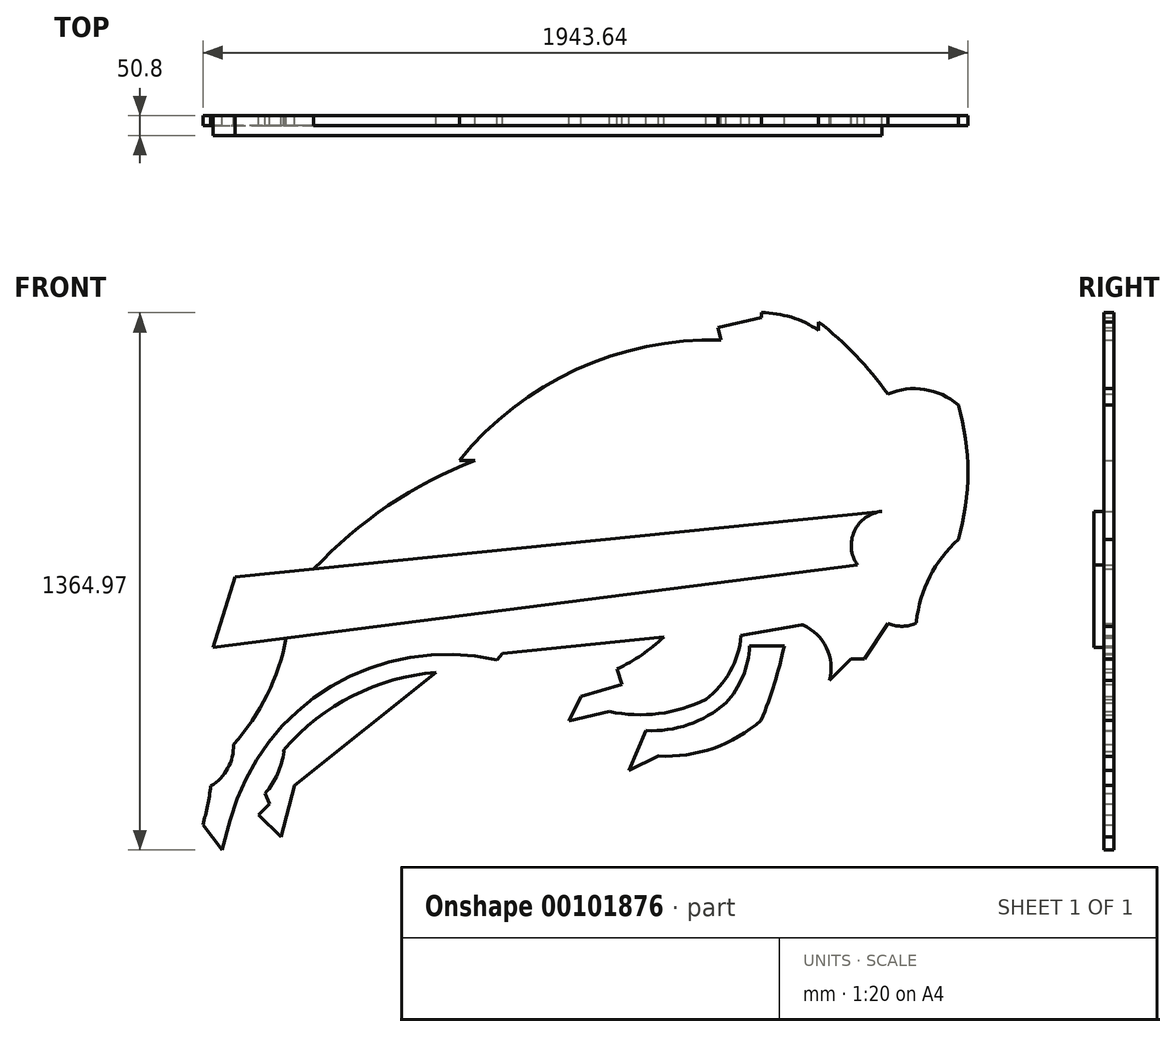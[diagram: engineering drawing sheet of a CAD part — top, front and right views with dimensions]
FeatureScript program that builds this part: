
annotation { "Feature Type Name" : "Feature", "Feature Type Description" : "" }
export const myFeature = defineFeature(function(context is Context, id is Id, definition is map)
    precondition{}
    {
        {
            var Q0;
            Q0=qCreatedBy(makeId("Front.planeOp"),FACE);
            var sketch = newSketch(context, id + "F0", { "sketchPlane" : qUnion([Q0])});
            skLineSegment(sketch, "E0", {"start": v(-973.64, 129.34) * mm, "end": v(-1030.7, -49.44) * mm});
            skLineSegment(sketch, "E1", {"start": v(-1030.7, -49.44) * mm, "end": v(606.92, 160.33) * mm});
            skLineSegment(sketch, "E2", {"start": v(-973.64, 129.34) * mm, "end": v(668.91, 296.17) * mm});
            skArc(sketch, "E3", {"start": v(668.91, 296.17) * mm, "mid": v(598.96, 246.03) * mm, "end": v(606.92, 160.33) * mm});
            skSolve(sketch);
        }
        {
            var Q0;
            Q0 = qSketchRegion(id + "F0", true);
            extrude(context, id + "F1", {"entities" : qUnion([Q0]), "depth" : 50.8 * mm});
        }
        {
            var Q0;
            Q0=makeQuery(id+"F1.opExtrude","CAP_FACE",FACE,{"disambiguationData":[OSD([sQuery(id+"F0.wireOp",EDGE,"E0"),sQuery(id+"F0.wireOp",EDGE,"E1"),sQuery(id+"F0.wireOp",EDGE,"E2"),sQuery(id+"F0.wireOp",EDGE,"E3")])],"isStart":false});
            var sketch = newSketch(context, id + "F2", { "sketchPlane" : qUnion([Q0])});
            skArc(sketch, "E4", {"start": v(260.08, 731.48) * mm, "mid": v(-108.02, 656.23) * mm, "end": v(-404.4, 425.33) * mm});
            skArc(sketch, "E5", {"start": v(-978.1, -295.87) * mm, "mid": v(-892.88, -169.79) * mm, "end": v(-844.3, -25.57) * mm});
            skArc(sketch, "E6", {"start": v(-1035.95, -401.48) * mm, "mid": v(-992.78, -356.48) * mm, "end": v(-978.1, -295.87) * mm});
            skLineSegment(sketch, "E7", {"start": v(-1006.96, -563.83) * mm, "end": v(-986.67, -488.45) * mm});
            skArc(sketch, "E8", {"start": v(-309.17, -81.5) * mm, "mid": v(-730, -148.32) * mm, "end": v(-986.67, -488.45) * mm});
            skLineSegment(sketch, "E9", {"start": v(-1006.96, -563.83) * mm, "end": v(-1056.25, -500.05) * mm});
            skArc(sketch, "E10", {"start": v(-1056.25, -500.05) * mm, "mid": v(-1044.13, -451.17) * mm, "end": v(-1035.95, -401.48) * mm});
            skLineSegment(sketch, "E11", {"start": v(-309.17, -81.5) * mm, "end": v(-295.02, -64.52) * mm});
            skLineSegment(sketch, "E12", {"start": v(-295.02, -64.52) * mm, "end": v(114.91, -22.89) * mm});
            skArc(sketch, "E13", {"start": v(-3.55, -103.77) * mm, "mid": v(58.9, -68.04) * mm, "end": v(114.91, -22.89) * mm});
            skLineSegment(sketch, "E14", {"start": v(-3.55, -103.77) * mm, "end": v(8.03, -143.56) * mm});
            skLineSegment(sketch, "E15", {"start": v(8.03, -143.56) * mm, "end": v(-95.54, -173.7) * mm});
            skLineSegment(sketch, "E16", {"start": v(-95.54, -173.7) * mm, "end": v(-126.44, -236.65) * mm});
            skLineSegment(sketch, "E17", {"start": v(-126.44, -236.65) * mm, "end": v(-23, -212.52) * mm});
            skArc(sketch, "E18", {"start": v(-23, -212.52) * mm, "mid": v(102, -217.48) * mm, "end": v(221.8, -181.49) * mm});
            skArc(sketch, "E19", {"start": v(221.8, -181.49) * mm, "mid": v(283.47, -109.79) * mm, "end": v(311.44, -19.44) * mm});
            skLineSegment(sketch, "E20", {"start": v(311.44, -19.44) * mm, "end": v(464.74, 7.81) * mm});
            skArc(sketch, "E21", {"start": v(535.54, -133.22) * mm, "mid": v(528.3, -50.32) * mm, "end": v(468.37, 7.4) * mm});
            skPoint(sketch, "E22.visualSharp", {"position": v(466.59, 8.14) * mm});
            skArc(sketch, "E22.filletArc", {"start": v(468.37, 7.4) * mm, "mid": v(466.58, 7.87) * mm, "end": v(464.74, 7.81) * mm});
            skLineSegment(sketch, "E23", {"start": v(535.54, -133.22) * mm, "end": v(590.7, -78.05) * mm});
            skLineSegment(sketch, "E24", {"start": v(590.7, -78.05) * mm, "end": v(625.19, -78.05) * mm});
            skLineSegment(sketch, "E25", {"start": v(625.19, -78.05) * mm, "end": v(683.8, 11.6) * mm});
            skArc(sketch, "E26", {"start": v(683.8, 11.6) * mm, "mid": v(717.53, 4.59) * mm, "end": v(751.58, 9.86) * mm});
            skArc(sketch, "E27", {"start": v(863.08, 224.87) * mm, "mid": v(790.65, 130.36) * mm, "end": v(756.67, 16.25) * mm});
            skPoint(sketch, "E28.visualSharp", {"position": v(756.2, 11.6) * mm});
            skArc(sketch, "E28.filletArc", {"start": v(751.58, 9.86) * mm, "mid": v(755.05, 12.32) * mm, "end": v(756.67, 16.25) * mm});
            skArc(sketch, "E29", {"start": v(863.08, 224.87) * mm, "mid": v(887.4, 395.78) * mm, "end": v(863.08, 566.69) * mm});
            skArc(sketch, "E30", {"start": v(863.08, 566.69) * mm, "mid": v(777.39, 606.14) * mm, "end": v(683.8, 594.27) * mm});
            skArc(sketch, "E31", {"start": v(683.8, 594.27) * mm, "mid": v(602.68, 692.55) * mm, "end": v(507.96, 777.8) * mm});
            skLineSegment(sketch, "E32", {"start": v(507.96, 777.8) * mm, "end": v(507.96, 756.32) * mm});
            skArc(sketch, "E33", {"start": v(507.96, 756.32) * mm, "mid": v(438.89, 789.48) * mm, "end": v(363.15, 801.14) * mm});
            skLineSegment(sketch, "E34", {"start": v(363.15, 801.14) * mm, "end": v(363.15, 788.44) * mm});
            skLineSegment(sketch, "E35", {"start": v(363.15, 788.44) * mm, "end": v(252.82, 763.21) * mm});
            skLineSegment(sketch, "E36", {"start": v(252.82, 763.21) * mm, "end": v(260.08, 731.48) * mm});
            skLineSegment(sketch, "E37", {"start": v(-404.4, 425.33) * mm, "end": v(-364.33, 425.33) * mm});
            skArc(sketch, "E38", {"start": v(-364.33, 425.33) * mm, "mid": v(-585.07, 310.89) * mm, "end": v(-774.28, 149.6) * mm});
            skSolve(sketch);
        }
        {
            var Q0;
            Q0 = qSketchRegion(id + "F2", true);
            var Q1;
            Q1=makeQuery(id+"F2.imprint","IMPRINT",FACE,{"disambiguationData":[TD([[makeQuery(id+"F2.imprint","IMPRINT",EDGE,{"derivedFrom":sQuery(id+"F2.wireOp",EDGE,"E4")}),1.0]])]});
            extrude(context, id + "F3", {"entities" : qUnion([Q0, Q1]), "depth" : 25.4 * mm});
        }
        {
            var Q0;
            Q0=makeQuery(id+"F1.opExtrude","CAP_FACE",FACE,{"disambiguationData":[OSD([sQuery(id+"F0.wireOp",EDGE,"E0"),sQuery(id+"F0.wireOp",EDGE,"E1"),sQuery(id+"F0.wireOp",EDGE,"E2"),sQuery(id+"F0.wireOp",EDGE,"E3")])],"isStart":false});
            var sketch = newSketch(context, id + "F4", { "sketchPlane" : qUnion([Q0])});
            skLineSegment(sketch, "E39", {"start": v(-973.64, 129.34) * mm, "end": v(-1030.7, -49.44) * mm});
            skLineSegment(sketch, "E40", {"start": v(-1030.7, -49.44) * mm, "end": v(606.92, 160.33) * mm});
            skLineSegment(sketch, "E41", {"start": v(-973.64, 129.34) * mm, "end": v(668.91, 296.17) * mm});
            skArc(sketch, "E42", {"start": v(668.91, 296.17) * mm, "mid": v(598.96, 246.03) * mm, "end": v(606.92, 160.33) * mm});
            skSolve(sketch);
        }
        {
            var Q0;
            Q0 = qSketchRegion(id + "F4", true);
            extrude(context, id + "F5", {"entities" : qUnion([Q0]), "depth" : 50.8 * mm});
        }
        {
            var Q0;
            Q0=makeQuery(id+"F1.opExtrude","CAP_FACE",FACE,{"disambiguationData":[OSD([sQuery(id+"F0.wireOp",EDGE,"E0"),sQuery(id+"F0.wireOp",EDGE,"E1"),sQuery(id+"F0.wireOp",EDGE,"E2"),sQuery(id+"F0.wireOp",EDGE,"E3")])],"isStart":true});
            var sketch = newSketch(context, id + "F6", { "sketchPlane" : qUnion([Q0])});
            skLineSegment(sketch, "E43", {"start": v(-668.91, 296.17) * mm, "end": v(973.64, 129.34) * mm});
            skLineSegment(sketch, "E44", {"start": v(973.64, 129.34) * mm, "end": v(1030.7, -49.44) * mm});
            skLineSegment(sketch, "E45", {"start": v(1030.7, -49.44) * mm, "end": v(-606.92, 160.33) * mm});
            skArc(sketch, "E46", {"start": v(-606.92, 160.33) * mm, "mid": v(-598.96, 246.03) * mm, "end": v(-668.91, 296.17) * mm});
            skSolve(sketch);
        }
        {
            var Q0;
            Q0=makeQuery(id+"F6.imprint","IMPRINT",FACE,{"disambiguationData":[TD([[makeQuery(id+"F6.imprint","IMPRINT",EDGE,{"derivedFrom":sQuery(id+"F6.wireOp",EDGE,"E43")}),1.0]])]});
            extrude(context, id + "F7", {"entities" : qUnion([Q0]), "operationType" : NewBodyOperationType.REMOVE, "oppositeDirection" : true, "depth" : 50.8 * mm});
        }
        {
            var Q0;
            Q0=makeQuery(id+"F3.opExtrude","CAP_FACE",FACE,{"disambiguationData":[OSD([sQuery(id+"F0.wireOp",EDGE,"E1"),sQuery(id+"F0.wireOp",EDGE,"E2"),sQuery(id+"F0.wireOp",EDGE,"E3"),sQuery(id+"F2.wireOp",EDGE,"E4"),sQuery(id+"F2.wireOp",EDGE,"E5"),sQuery(id+"F2.wireOp",EDGE,"E6"),sQuery(id+"F2.wireOp",EDGE,"E7"),sQuery(id+"F2.wireOp",EDGE,"E8"),sQuery(id+"F2.wireOp",EDGE,"E9"),sQuery(id+"F2.wireOp",EDGE,"E10"),sQuery(id+"F2.wireOp",EDGE,"E11"),sQuery(id+"F2.wireOp",EDGE,"E12"),sQuery(id+"F2.wireOp",EDGE,"E13"),sQuery(id+"F2.wireOp",EDGE,"E14"),sQuery(id+"F2.wireOp",EDGE,"E15"),sQuery(id+"F2.wireOp",EDGE,"E16"),sQuery(id+"F2.wireOp",EDGE,"E17"),sQuery(id+"F2.wireOp",EDGE,"E18"),sQuery(id+"F2.wireOp",EDGE,"E19"),sQuery(id+"F2.wireOp",EDGE,"E20"),sQuery(id+"F2.wireOp",EDGE,"E21"),sQuery(id+"F2.wireOp",EDGE,"E22.filletArc"),sQuery(id+"F2.wireOp",EDGE,"E23"),sQuery(id+"F2.wireOp",EDGE,"E24"),sQuery(id+"F2.wireOp",EDGE,"E25"),sQuery(id+"F2.wireOp",EDGE,"E26"),sQuery(id+"F2.wireOp",EDGE,"E27"),sQuery(id+"F2.wireOp",EDGE,"E28.filletArc"),sQuery(id+"F2.wireOp",EDGE,"E29"),sQuery(id+"F2.wireOp",EDGE,"E30"),sQuery(id+"F2.wireOp",EDGE,"E31"),sQuery(id+"F2.wireOp",EDGE,"E32"),sQuery(id+"F2.wireOp",EDGE,"E33"),sQuery(id+"F2.wireOp",EDGE,"E34"),sQuery(id+"F2.wireOp",EDGE,"E35"),sQuery(id+"F2.wireOp",EDGE,"E36"),sQuery(id+"F2.wireOp",EDGE,"E37"),sQuery(id+"F2.wireOp",EDGE,"E38")])],"isStart":true});
            var sketch = newSketch(context, id + "F8", { "sketchPlane" : qUnion([Q0])});
            skArc(sketch, "E47", {"start": v(848.7, -307.72) * mm, "mid": v(675.35, -172.47) * mm, "end": v(463.75, -112.7) * mm});
            skLineSegment(sketch, "E48", {"start": v(463.75, -112.7) * mm, "end": v(823.31, -399.79) * mm});
            skLineSegment(sketch, "E49", {"start": v(823.31, -399.79) * mm, "end": v(857.97, -531.17) * mm});
            skLineSegment(sketch, "E50", {"start": v(857.97, -531.17) * mm, "end": v(914.31, -474.82) * mm});
            skLineSegment(sketch, "E51", {"start": v(914.31, -474.82) * mm, "end": v(886.14, -446.64) * mm});
            skPoint(sketch, "E51.endSnap0", {"position": v(886.14, -503) * mm});
            skLineSegment(sketch, "E52", {"start": v(886.14, -446.64) * mm, "end": v(897.64, -419.94) * mm});
            skPoint(sketch, "E53.visualSharp", {"position": v(851.18, -310.6) * mm});
            skArc(sketch, "E53.filletArc", {"start": v(850.43, -314.15) * mm, "mid": v(850.31, -310.73) * mm, "end": v(848.7, -307.72) * mm});
            skArc(sketch, "E54", {"start": v(850.43, -314.15) * mm, "mid": v(866.26, -370.52) * mm, "end": v(897.64, -419.94) * mm});
            skArc(sketch, "E55", {"start": v(-333.12, -45.55) * mm, "mid": v(-315.58, -123.35) * mm, "end": v(-272.34, -190.36) * mm});
            skLineSegment(sketch, "E56", {"start": v(-69.25, -260.42) * mm, "end": v(-26.92, -361.34) * mm});
            skLineSegment(sketch, "E57", {"start": v(-26.92, -361.34) * mm, "end": v(-101.8, -325.53) * mm});
            skLineSegment(sketch, "E58", {"start": v(-333.12, -45.55) * mm, "end": v(-420.84, -45.55) * mm});
            skArc(sketch, "E59", {"start": v(-420.84, -45.55) * mm, "mid": v(-395.92, -141.32) * mm, "end": v(-362.24, -234.37) * mm});
            skArc(sketch, "E60", {"start": v(-362.24, -234.37) * mm, "mid": v(-240.92, -305.37) * mm, "end": v(-101.8, -325.53) * mm});
            skPoint(sketch, "E61", {"position": v(-272.34, -190.36) * mm});
            skArc(sketch, "E62", {"start": v(-272.34, -190.36) * mm, "mid": v(-177.66, -245.3) * mm, "end": v(-69.25, -260.42) * mm});
            skSolve(sketch);
        }
        {
            var Q0;
            Q0 = qSketchRegion(id + "F8", true);
            extrude(context, id + "F9", {"entities" : qUnion([Q0]), "depth" : 25.4 * mm});
        }
        {
            var Q0;
            Q0=makeQuery(id+"F9.opExtrude","CAP_FACE",FACE,{"disambiguationData":[OSD([sQuery(id+"F8.wireOp",EDGE,"E47"),sQuery(id+"F8.wireOp",EDGE,"E48"),sQuery(id+"F8.wireOp",EDGE,"E49"),sQuery(id+"F8.wireOp",EDGE,"E50"),sQuery(id+"F8.wireOp",EDGE,"E51"),sQuery(id+"F8.wireOp",EDGE,"E52"),sQuery(id+"F8.wireOp",EDGE,"E53.filletArc"),sQuery(id+"F8.wireOp",EDGE,"E54")])],"isStart":true});
            var sketch = newSketch(context, id + "F10", { "sketchPlane" : qUnion([Q0])});
            skArc(sketch, "E63.0", {"start": v(-463.75, -112.7) * mm, "mid": v(-675.35, -172.47) * mm, "end": v(-848.7, -307.72) * mm});
            skLineSegment(sketch, "E63.1", {"start": v(-823.31, -399.79) * mm, "end": v(-463.75, -112.7) * mm});
            skArc(sketch, "E63.2", {"start": v(-848.7, -307.72) * mm, "mid": v(-850.31, -310.73) * mm, "end": v(-850.43, -314.15) * mm});
            skLineSegment(sketch, "E63.3", {"start": v(-857.97, -531.17) * mm, "end": v(-823.31, -399.79) * mm});
            skArc(sketch, "E63.4", {"start": v(-850.43, -314.15) * mm, "mid": v(-866.26, -370.52) * mm, "end": v(-897.64, -419.94) * mm});
            skLineSegment(sketch, "E63.5", {"start": v(-897.64, -419.94) * mm, "end": v(-886.14, -446.64) * mm});
            skLineSegment(sketch, "E63.6", {"start": v(-886.14, -446.64) * mm, "end": v(-914.31, -474.82) * mm});
            skLineSegment(sketch, "E63.7", {"start": v(-914.31, -474.82) * mm, "end": v(-857.97, -531.17) * mm});
            skLineSegment(sketch, "E64.0", {"start": v(420.84, -45.55) * mm, "end": v(333.12, -45.55) * mm});
            skArc(sketch, "E64.1", {"start": v(362.24, -234.37) * mm, "mid": v(395.92, -141.32) * mm, "end": v(420.84, -45.55) * mm});
            skArc(sketch, "E64.2", {"start": v(272.34, -190.36) * mm, "mid": v(177.66, -245.3) * mm, "end": v(69.25, -260.42) * mm});
            skLineSegment(sketch, "E64.3", {"start": v(69.25, -260.42) * mm, "end": v(26.92, -361.34) * mm});
            skLineSegment(sketch, "E64.4", {"start": v(26.92, -361.34) * mm, "end": v(101.8, -325.53) * mm});
            skArc(sketch, "E64.5", {"start": v(333.12, -45.55) * mm, "mid": v(315.58, -123.35) * mm, "end": v(272.34, -190.36) * mm});
            skArc(sketch, "E64.6", {"start": v(101.8, -325.53) * mm, "mid": v(240.92, -305.37) * mm, "end": v(362.24, -234.37) * mm});
            skSolve(sketch);
        }
        {
            var Q0;
            Q0=makeQuery(id+"F10.imprint","IMPRINT",FACE,{"disambiguationData":[TD([[makeQuery(id+"F10.imprint","IMPRINT",EDGE,{"derivedFrom":sQuery(id+"F10.wireOp",EDGE,"E63.0")}),-1.0]])]});
            var Q1;
            Q1=makeQuery(id+"F10.imprint","IMPRINT",FACE,{"disambiguationData":[TD([[makeQuery(id+"F10.imprint","IMPRINT",EDGE,{"derivedFrom":sQuery(id+"F10.wireOp",EDGE,"E64.0")}),1.0]])]});
            extrude(context, id + "F11", {"entities" : qUnion([Q0, Q1]), "depth" : 25.4 * mm});
        }
        {
            var Q0;
            Q0=makeQuery(id+"F9.opExtrude","CAP_FACE",FACE,{"disambiguationData":[OSD([sQuery(id+"F8.wireOp",EDGE,"E47"),sQuery(id+"F8.wireOp",EDGE,"E48"),sQuery(id+"F8.wireOp",EDGE,"E49"),sQuery(id+"F8.wireOp",EDGE,"E50"),sQuery(id+"F8.wireOp",EDGE,"E51"),sQuery(id+"F8.wireOp",EDGE,"E52"),sQuery(id+"F8.wireOp",EDGE,"E53.filletArc"),sQuery(id+"F8.wireOp",EDGE,"E54")])],"isStart":false});
            var sketch = newSketch(context, id + "F12", { "sketchPlane" : qUnion([Q0])});
            skArc(sketch, "E65.0", {"start": v(897.64, -419.94) * mm, "mid": v(866.26, -370.52) * mm, "end": v(850.43, -314.15) * mm});
            skLineSegment(sketch, "E65.1", {"start": v(886.14, -446.64) * mm, "end": v(897.64, -419.94) * mm});
            skArc(sketch, "E65.2", {"start": v(850.43, -314.15) * mm, "mid": v(850.31, -310.73) * mm, "end": v(848.7, -307.72) * mm});
            skLineSegment(sketch, "E65.3", {"start": v(914.31, -474.82) * mm, "end": v(886.14, -446.64) * mm});
            skArc(sketch, "E65.4", {"start": v(848.7, -307.72) * mm, "mid": v(675.35, -172.47) * mm, "end": v(463.75, -112.7) * mm});
            skLineSegment(sketch, "E65.5", {"start": v(463.75, -112.7) * mm, "end": v(823.31, -399.79) * mm});
            skLineSegment(sketch, "E65.6", {"start": v(823.31, -399.79) * mm, "end": v(857.97, -531.17) * mm});
            skLineSegment(sketch, "E65.7", {"start": v(857.97, -531.17) * mm, "end": v(914.31, -474.82) * mm});
            skArc(sketch, "E66.0", {"start": v(-69.25, -260.42) * mm, "mid": v(-177.66, -245.3) * mm, "end": v(-272.34, -190.36) * mm});
            skLineSegment(sketch, "E66.1", {"start": v(-26.92, -361.34) * mm, "end": v(-69.25, -260.42) * mm});
            skLineSegment(sketch, "E66.2", {"start": v(-333.12, -45.55) * mm, "end": v(-420.84, -45.55) * mm});
            skArc(sketch, "E66.3", {"start": v(-420.84, -45.55) * mm, "mid": v(-395.92, -141.32) * mm, "end": v(-362.24, -234.37) * mm});
            skArc(sketch, "E66.4", {"start": v(-362.24, -234.37) * mm, "mid": v(-240.92, -305.37) * mm, "end": v(-101.8, -325.53) * mm});
            skArc(sketch, "E66.5", {"start": v(-272.34, -190.36) * mm, "mid": v(-315.58, -123.35) * mm, "end": v(-333.12, -45.55) * mm});
            skLineSegment(sketch, "E66.6", {"start": v(-101.8, -325.53) * mm, "end": v(-26.92, -361.34) * mm});
            skSolve(sketch);
        }
        {
            var Q0;
            Q0=makeQuery(id+"F12.imprint","IMPRINT",FACE,{"disambiguationData":[TD([[makeQuery(id+"F12.imprint","IMPRINT",EDGE,{"derivedFrom":sQuery(id+"F12.wireOp",EDGE,"E65.0")}),-1.0]])]});
            var Q1;
            Q1=makeQuery(id+"F12.imprint","IMPRINT",FACE,{"disambiguationData":[TD([[makeQuery(id+"F12.imprint","IMPRINT",EDGE,{"derivedFrom":sQuery(id+"F12.wireOp",EDGE,"E66.0")}),1.0]])]});
            extrude(context, id + "F13", {"entities" : qUnion([Q0, Q1]), "operationType" : NewBodyOperationType.REMOVE, "oppositeDirection" : true, "depth" : 25.4 * mm});
        }
        {
            var Q0;
            Q0=makeQuery(id+"F9.opExtrude","CAP_FACE",FACE,{"disambiguationData":[OSD([sQuery(id+"F8.wireOp",EDGE,"E55"),sQuery(id+"F8.wireOp",EDGE,"E56"),sQuery(id+"F8.wireOp",EDGE,"E57"),sQuery(id+"F8.wireOp",EDGE,"E58"),sQuery(id+"F8.wireOp",EDGE,"E59"),sQuery(id+"F8.wireOp",EDGE,"E60"),sQuery(id+"F8.wireOp",EDGE,"E62")])],"isStart":false});
            var sketch = newSketch(context, id + "F14", { "sketchPlane" : qUnion([Q0])});
            skArc(sketch, "E67.0", {"start": v(-69.25, -260.42) * mm, "mid": v(-177.66, -245.3) * mm, "end": v(-272.34, -190.36) * mm});
            skLineSegment(sketch, "E67.1", {"start": v(-26.92, -361.34) * mm, "end": v(-69.25, -260.42) * mm});
            skLineSegment(sketch, "E67.2", {"start": v(-333.12, -45.55) * mm, "end": v(-420.84, -45.55) * mm});
            skArc(sketch, "E67.3", {"start": v(-420.84, -45.55) * mm, "mid": v(-395.92, -141.32) * mm, "end": v(-362.24, -234.37) * mm});
            skArc(sketch, "E67.4", {"start": v(-362.24, -234.37) * mm, "mid": v(-240.92, -305.37) * mm, "end": v(-101.8, -325.53) * mm});
            skArc(sketch, "E67.5", {"start": v(-272.34, -190.36) * mm, "mid": v(-315.58, -123.35) * mm, "end": v(-333.12, -45.55) * mm});
            skLineSegment(sketch, "E67.6", {"start": v(-101.8, -325.53) * mm, "end": v(-26.92, -361.34) * mm});
            skSolve(sketch);
        }
        {
            var Q0;
            Q0=makeQuery(id+"F14.imprint","IMPRINT",FACE,{"disambiguationData":[TD([[makeQuery(id+"F14.imprint","IMPRINT",EDGE,{"derivedFrom":sQuery(id+"F14.wireOp",EDGE,"E67.0")}),-1.0]])]});
            extrude(context, id + "F15", {"entities" : qUnion([Q0]), "operationType" : NewBodyOperationType.REMOVE, "oppositeDirection" : true, "depth" : 25.4 * mm});
        }
    });
